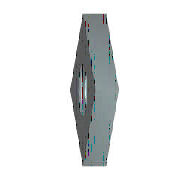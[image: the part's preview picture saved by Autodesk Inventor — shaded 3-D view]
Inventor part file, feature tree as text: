
AUTODESK INVENTOR PART (.ipt)
format: ipt  version: 2013 (Build 170138000, 138)  size: 122,880 bytes
history: native  units: mm (DEFAULTED — no unit token found)
features: sketch x2, hole x1, other x1, plane x1
ambient origin geometry x8: Origin, YZ Plane, XZ Plane, XY Plane, X Axis, Y Axis, Z Axis, Center Point
bodies: Solid1 (feature_tree), Body (feature_tree)
feature tree (5):
  hole  "Thread"  [1 undecoded]
  other  "Work Axis1"
  plane  "Work Plane1"
  sketch  "Sketch1"  dims[d0=7.778175mm d1=1.8mm d2=0.0mm]
  sketch  "Sketch2"  dims[d20=2.459mm d21=6.0mm d22=4.0mm d23=2.0mm d24=14.3117mm d25=8.0mm d26=20.594885mm d3=0.270633mm d4=30.0deg d5=0.270633mm d6=30.0deg d8=0.0mm d9=0.0mm d34=0.0mm d35=0.270633mm d36=0.270633mm d37=90.0deg d38=0.0mm]
note: 1 required parameter value undecoded (feature->parameter linkage not recoverable at this tier; creation-order binding heuristic only, values carry confidence <= 0.55)
